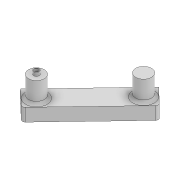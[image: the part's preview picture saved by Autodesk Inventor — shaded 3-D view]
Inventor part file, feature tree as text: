
AUTODESK INVENTOR PART (.ipt)
format: ipt  version: 2022 (Build 260153000, 153)  size: 281,600 bytes
history: native  units: in
note: dims shown in document units (in); Inventor stores cm internally (conversion verified against a paired STEP export)
features: extrude x15, sketch x13, projected_geometry x9, plane x5, other x5, reference x4, fillet x3, mirror x1
ambient origin geometry x8: Origin, YZ Plane, XZ Plane, XY Plane, X Axis, Y Axis, Z Axis, Center Point
bodies: Solid1 (feature_tree)
feature tree (55):
  extrude  "Extrusion1"  Depth=1.9685in
  extrude  "Extrusion2"  Depth=0.1181in
  extrude  "Extrusion3"  Depth=0.5906in
  sketch  "Sketch5"  dims[d7=1.1811in d8=0.9843in]
  extrude  "Extrusion5"  Depth=0.9843in
  extrude  "Extrusion6"  Depth=0.7087in TaperAngle=0.0deg
  plane  "Work Plane1"
  extrude  "Extrusion7"  Depth=0.1929in
  extrude  "Extrusion8"  Depth=0.1181in
  extrude  "Extrusion9"  Depth=1.9685in TaperAngle=0.0deg
  fillet  "Fillet1"  Radius=0.0079in
  fillet  "Fillet2"  Radius=0.0079in
  sketch  "Sketch11"  dims[d29=0.7874in d30=0.0984in]
  extrude  "Extrusion10"  Depth=0.0984in
  sketch  "Sketch12"  dims[d31=0.0984in d32=0.7874in]
  plane  "Work Plane2"
  extrude  "Extrusion11"  Depth=0.7874in
  extrude  "Extrusion12"  Depth=0.0984in
  fillet  "Fillet3"  [1 undecoded]
  plane  "Work Plane3"
  mirror  "Mirror1"
  sketch  "Sketch14"  dims[d37=0.0984in d38=0.252in d39=0.0in]
  plane  "Work Plane4"
  extrude  "Extrusion13"  Depth=0.252in TaperAngle=0.0deg
  sketch  "Sketch15"  dims[d40=0.0984in d41=0.0in d42=0.0984in d43=0.0984in d44=0.3228in d45=0.0591in d46=0.0in d47=2.5268in d48=0.0in d49=0.0984in d50=0.0in d51=0.0984in d52=-1.7063in d53=0.0984in d54=0.0in d55=0.3937in d56=0.0in d57=0.0591in d58=0.0in d59=0.0591in d60=0.0in]
  plane  "Work Plane5"
  extrude  "Extrusion14"  Depth=0.0984in
  extrude  "Extrusion15"  Depth=0.0984in
  extrude  "Extrusion16"  Depth=0.3228in
  sketch  "Sketch1"  dims[d0=3.937in d1=1.9685in]
  sketch  "Sketch2"  dims[d2=0.1181in d3=0.0in d4=0.5512in]
  sketch  "Sketch3"  dims[d5=0.5512in d6=0.5906in]
  projected_geometry  "Projected Loop1"
  projected_geometry  "Projected Loop2"
  sketch  "Sketch7"  dims[d9=0.9843in d10=0.7087in d11=0.0in]
  projected_geometry  "Projected Loop4"
  sketch  "Sketch8"  dims[d12=0.2264in d13=0.1929in]
  reference  "Reference1"
  reference  "Reference2"
  reference  "Reference3"
  reference  "Reference4"
  sketch  "Sketch9"  dims[d14=0.1181in d15=0.0in d20=0.1516in]
  projected_geometry  "Projected Loop5"
  sketch  "Sketch10"  dims[d21=0.5906in d22=0.0in d24=1.9685in d25=0.0in d26=0.0079in d27=0.0079in]
  projected_geometry  "Projected Loop6"
  projected_geometry  "Projected Loop7"
  projected_geometry  "Projected Loop8"
  sketch  "Sketch13"  dims[d33=0.0984in d34=0.0in d35=0.0984in d36=0.0in]
  projected_geometry  "Projected Loop9"
  projected_geometry  "Projected Loop10"
  other  "<userpath>\OneDrive\Desktop\P3\2. Hopper Assembly\Updated_Hopper_Mechanism.iam"
  other  "Updated_Hopper_Mechanism.iam"
  other  "Connecting_Plate:1"
  other  "HopperVR41Y_Base:1"
  other  "92095A199_Button Head Hex Drive Screw:1"
note: 1 required parameter value undecoded (feature->parameter linkage not recoverable at this tier; creation-order binding heuristic only, values carry confidence <= 0.55)
